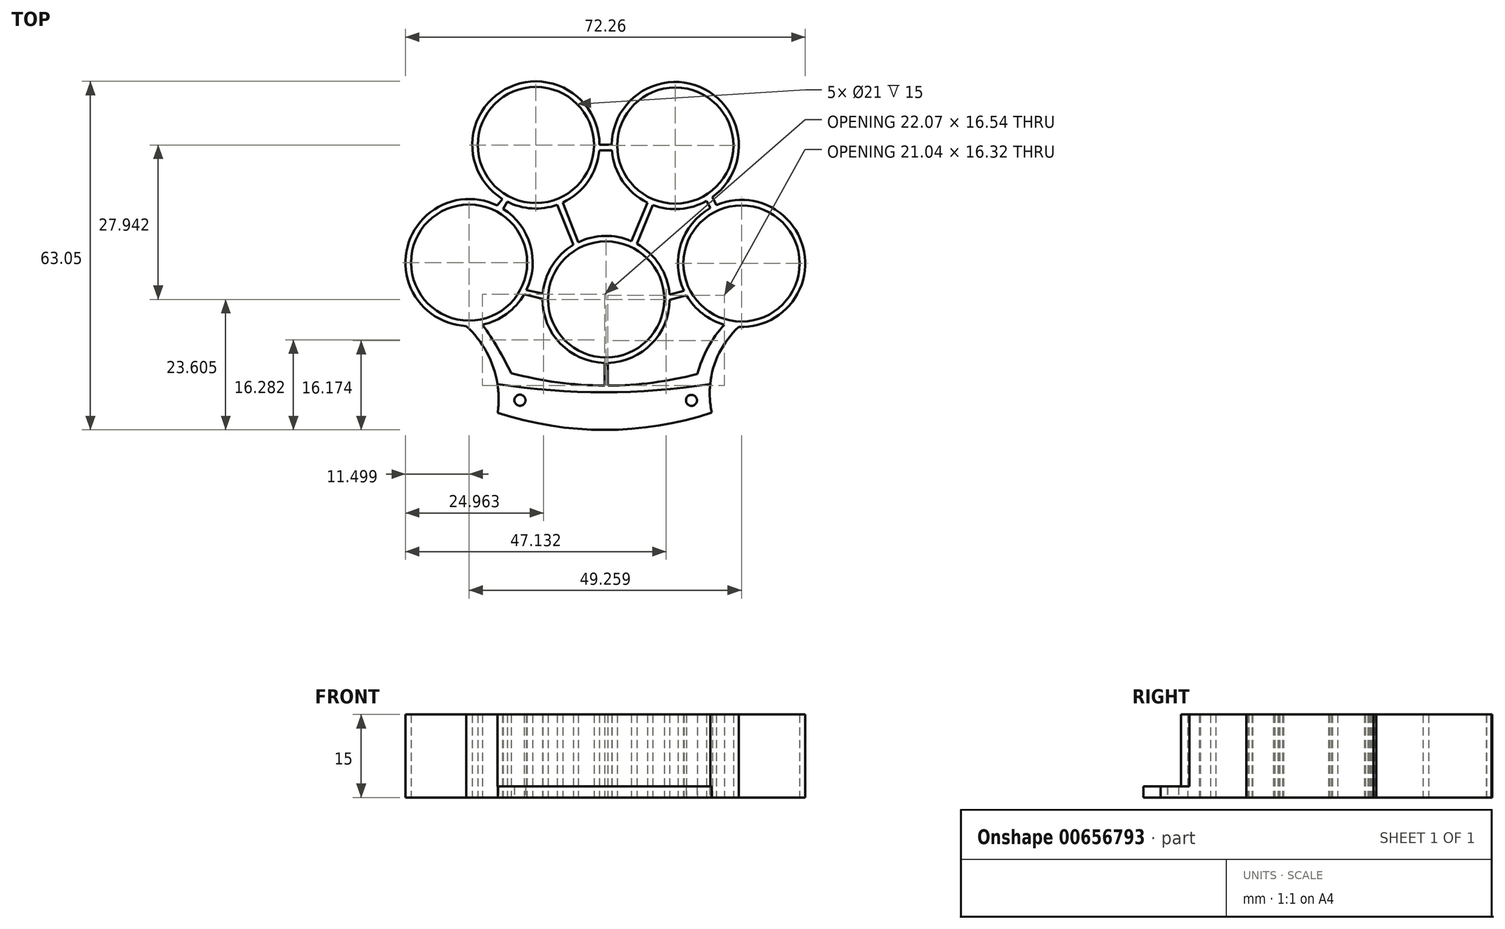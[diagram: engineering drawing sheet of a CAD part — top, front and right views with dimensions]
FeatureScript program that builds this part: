
annotation { "Feature Type Name" : "Feature", "Feature Type Description" : "" }
export const myFeature = defineFeature(function(context is Context, id is Id, definition is map)
    precondition{}
    {
        {
            var Q0;
            Q0=qCreatedBy(makeId("Top.planeOp"),FACE);
            var sketch = newSketch(context, id + "F0", { "sketchPlane" : qUnion([Q0])});
            skCircle(sketch, "E0", {"center": v(0, 0) * mm, "radius": 65 * mm, "construction": true});
            skCircle(sketch, "E1", {"center": v(0, 0) * mm, "radius": 49.37 * mm, "construction": true});
            skCircle(sketch, "E2", {"center": v(-24.77, -42.7) * mm, "radius": 10.5 * mm});
            skCircle(sketch, "E3", {"center": v(0, -49.37) * mm, "radius": 10.5 * mm});
            skCircle(sketch, "E4", {"center": v(24.49, -42.86) * mm, "radius": 10.5 * mm});
            skCircle(sketch, "E5", {"center": v(0, 0) * mm, "radius": 24.9 * mm, "construction": true});
            skLineSegment(sketch, "E6", {"start": v(0, 0) * mm, "end": v(95.97, 0) * mm, "construction": true});
            skLineSegment(sketch, "E7", {"start": v(0, 0) * mm, "end": v(-94.56, 0) * mm, "construction": true});
            skCircle(sketch, "E8", {"center": v(12.52, -21.53) * mm, "radius": 11.5 * mm});
            skCircle(sketch, "E9", {"center": v(-12.7, -21.42) * mm, "radius": 11.5 * mm});
            skLineSegment(sketch, "E10", {"start": v(-89.55, 88.06) * mm, "end": v(89.42, 88.01) * mm, "construction": true});
            skCircle(sketch, "E11", {"center": v(-15.57, -67.61) * mm, "radius": 1 * mm});
            skCircle(sketch, "E12", {"center": v(15.44, -67.63) * mm, "radius": 1 * mm});
            skCircle(sketch, "E13", {"center": v(24.49, -42.86) * mm, "radius": 11.5 * mm});
            skCircle(sketch, "E14", {"center": v(0, -49.37) * mm, "radius": 11.5 * mm});
            skCircle(sketch, "E15", {"center": v(-24.77, -42.7) * mm, "radius": 11.5 * mm});
            skCircle(sketch, "E16", {"center": v(-12.7, -21.42) * mm, "radius": 10.5 * mm});
            skCircle(sketch, "E17", {"center": v(12.52, -21.53) * mm, "radius": 10.5 * mm});
            skArc(sketch, "E18", {"start": v(-19.58, -69.88) * mm, "mid": v(-0.23, -72.97) * mm, "end": v(19.12, -69.83) * mm});
            skArc(sketch, "E19", {"start": v(-19.58, -69.88) * mm, "mid": v(-20.5, -61.33) * mm, "end": v(-25.28, -54.19) * mm});
            skArc(sketch, "E20", {"start": v(23.98, -54.35) * mm, "mid": v(19.48, -61.44) * mm, "end": v(19.12, -69.83) * mm});
            skArc(sketch, "E21", {"start": v(-17.15, -62.7) * mm, "mid": v(-0.33, -64.96) * mm, "end": v(16.5, -62.87) * mm});
            skLineSegment(sketch, "E22", {"start": v(-0.27, -60.86) * mm, "end": v(-0.27, -64.96) * mm});
            skLineSegment(sketch, "E23", {"start": v(0.34, -60.86) * mm, "end": v(0.34, -64.96) * mm});
            skArc(sketch, "E24", {"start": v(21.38, -53.94) * mm, "mid": v(18.4, -58.1) * mm, "end": v(16.5, -62.87) * mm});
            skArc(sketch, "E25", {"start": v(-17.15, -62.7) * mm, "mid": v(-19.57, -58.21) * mm, "end": v(-22.34, -53.94) * mm});
            skLineSegment(sketch, "E26", {"start": v(11.47, -48.51) * mm, "end": v(14.1, -47.8) * mm});
            skLineSegment(sketch, "E27", {"start": v(14.54, -48.63) * mm, "end": v(11.5, -49.47) * mm});
            skLineSegment(sketch, "E28", {"start": v(-14.4, -47.66) * mm, "end": v(-11.45, -48.32) * mm});
            skLineSegment(sketch, "E29", {"start": v(-14.8, -48.42) * mm, "end": v(-11.5, -49.26) * mm});
            skLineSegment(sketch, "E30", {"start": v(-1.2, -21.38) * mm, "end": v(1.02, -21.38) * mm});
            skLineSegment(sketch, "E31", {"start": v(1.05, -22.4) * mm, "end": v(-1.23, -22.4) * mm});
            skLineSegment(sketch, "E32", {"start": v(-19.67, -32.4) * mm, "end": v(-18.75, -31.2) * mm});
            skLineSegment(sketch, "E33", {"start": v(-17.88, -31.69) * mm, "end": v(-18.63, -32.98) * mm});
            skLineSegment(sketch, "E34", {"start": v(18.16, -31.54) * mm, "end": v(18.88, -32.83) * mm});
            skLineSegment(sketch, "E35", {"start": v(19.23, -30.86) * mm, "end": v(19.92, -32.3) * mm});
            skLineSegment(sketch, "E36", {"start": v(4.6, -38.82) * mm, "end": v(7.46, -31.85) * mm});
            skLineSegment(sketch, "E37", {"start": v(8.46, -32.29) * mm, "end": v(5.6, -39.32) * mm});
            skLineSegment(sketch, "E38", {"start": v(-5.03, -39.03) * mm, "end": v(-7.85, -31.85) * mm});
            skLineSegment(sketch, "E39", {"start": v(-8.85, -32.26) * mm, "end": v(-5.91, -39.5) * mm});
            skLineSegment(sketch, "E40", {"start": v(0, 0) * mm, "end": v(12.48, -6.94) * mm});
            skLineSegment(sketch, "E41", {"start": v(12.48, -6.94) * mm, "end": v(21.83, -11.98) * mm});
            skLineSegment(sketch, "E42", {"start": v(21.83, -11.98) * mm, "end": v(35.02, -34.8) * mm});
            skLineSegment(sketch, "E43", {"start": v(35.02, -34.8) * mm, "end": v(46.04, -45.89) * mm});
            skLineSegment(sketch, "E44", {"start": v(0, 0) * mm, "end": v(-21.9, -11.84) * mm});
            skLineSegment(sketch, "E45", {"start": v(-21.9, -11.84) * mm, "end": v(-35.08, -34.73) * mm});
            skLineSegment(sketch, "E46", {"start": v(-35.08, -34.73) * mm, "end": v(-46.2, -45.72) * mm});
            skLineSegment(sketch, "E47", {"start": v(-46.2, -45.72) * mm, "end": v(-49.24, -48.95) * mm});
            skLineSegment(sketch, "E48", {"start": v(-49.24, -48.95) * mm, "end": v(-19.58, -69.88) * mm});
            skLineSegment(sketch, "E49", {"start": v(46.04, -45.89) * mm, "end": v(48.99, -48.77) * mm});
            skLineSegment(sketch, "E50", {"start": v(48.99, -48.77) * mm, "end": v(19.12, -69.83) * mm});
            skSolve(sketch);
        }
        {
            var Q0;
            {var subQ0=sQuery(id+"F0.wireOp",EDGE,"E36");Q0=makeQuery(id+"F0.imprint","IMPRINT",FACE,{"disambiguationData":[TD([[makeQuery(id+"F0.imprint","IMPRINT",EDGE,{"derivedFrom":subQ0}),-1.0]])]});}
            var Q1;
            Q1=makeQuery(id+"F0.imprint","IMPRINT",FACE,{"disambiguationData":[TD([[makeQuery(id+"F0.imprint","IMPRINT",EDGE,{"derivedFrom":sQuery(id+"F0.wireOp",EDGE,"E3")}),-1.0]])]});
            var Q2;
            {var subQ0=sQuery(id+"F0.wireOp",EDGE,"E38");Q2=makeQuery(id+"F0.imprint","IMPRINT",FACE,{"disambiguationData":[TD([[makeQuery(id+"F0.imprint","IMPRINT",EDGE,{"derivedFrom":subQ0}),1.0]])]});}
            var Q3;
            {var subQ0=sQuery(id+"F0.wireOp",EDGE,"E28");Q3=makeQuery(id+"F0.imprint","IMPRINT",FACE,{"disambiguationData":[TD([[makeQuery(id+"F0.imprint","IMPRINT",EDGE,{"derivedFrom":subQ0}),-1.0]])]});}
            var Q4;
            {var subQ0=sQuery(id+"F0.wireOp",EDGE,"E22");Q4=makeQuery(id+"F0.imprint","IMPRINT",FACE,{"disambiguationData":[TD([[makeQuery(id+"F0.imprint","IMPRINT",EDGE,{"derivedFrom":subQ0}),1.0]])]});}
            var Q5;
            {var subQ0=sQuery(id+"F0.wireOp",EDGE,"E26");Q5=makeQuery(id+"F0.imprint","IMPRINT",FACE,{"disambiguationData":[TD([[makeQuery(id+"F0.imprint","IMPRINT",EDGE,{"derivedFrom":subQ0}),-1.0]])]});}
            var Q6;
            Q6 = qSketchRegion(id + "F2", true);
            var Q7;
            Q7=makeQuery(id+"F0.imprint","IMPRINT",FACE,{"disambiguationData":[TD([[makeQuery(id+"F0.imprint","IMPRINT",EDGE,{"derivedFrom":sQuery(id+"F0.wireOp",EDGE,"E2")}),-1.0]])]});
            var Q8;
            Q8=makeQuery(id+"F0.imprint","IMPRINT",FACE,{"disambiguationData":[TD([[makeQuery(id+"F0.imprint","IMPRINT",EDGE,{"derivedFrom":sQuery(id+"F0.wireOp",EDGE,"E11")}),-1.0]])]});
            var Q9;
            Q9=makeQuery(id+"F0.imprint","IMPRINT",FACE,{"disambiguationData":[TD([[makeQuery(id+"F0.imprint","IMPRINT",EDGE,{"derivedFrom":sQuery(id+"F0.wireOp",EDGE,"E16")}),-1.0]])]});
            var Q10;
            {var subQ0=sQuery(id+"F0.wireOp",EDGE,"E32");Q10=makeQuery(id+"F0.imprint","IMPRINT",FACE,{"disambiguationData":[TD([[makeQuery(id+"F0.imprint","IMPRINT",EDGE,{"derivedFrom":subQ0}),-1.0]])]});}
            var Q11;
            {var subQ0=sQuery(id+"F0.wireOp",EDGE,"E30");Q11=makeQuery(id+"F0.imprint","IMPRINT",FACE,{"disambiguationData":[TD([[makeQuery(id+"F0.imprint","IMPRINT",EDGE,{"derivedFrom":subQ0}),-1.0]])]});}
            var Q12;
            Q12=makeQuery(id+"F0.imprint","IMPRINT",FACE,{"disambiguationData":[TD([[makeQuery(id+"F0.imprint","IMPRINT",EDGE,{"derivedFrom":sQuery(id+"F0.wireOp",EDGE,"E17")}),-1.0]])]});
            var Q13;
            {var subQ0=sQuery(id+"F0.wireOp",EDGE,"E34");Q13=makeQuery(id+"F0.imprint","IMPRINT",FACE,{"disambiguationData":[TD([[makeQuery(id+"F0.imprint","IMPRINT",EDGE,{"derivedFrom":subQ0}),1.0]])]});}
            var Q14;
            Q14=makeQuery(id+"F0.imprint","IMPRINT",FACE,{"disambiguationData":[TD([[makeQuery(id+"F0.imprint","IMPRINT",EDGE,{"derivedFrom":sQuery(id+"F0.wireOp",EDGE,"E4")}),-1.0]])]});
            extrude(context, id + "F1", {"entities" : qUnion([Q0, Q1, Q2, Q3, Q4, Q5, Q6, Q7, Q8, Q9, Q10, Q11, Q12, Q13, Q14]), "depth" : 15 * mm, "offsetDistance" : 25 * mm});
        }
        {
            var Q0;
            Q0=makeQuery(id+"F1.opExtrude","CAP_FACE",FACE,{"disambiguationData":[OSD([sQuery(id+"F0.wireOp",EDGE,"E2"),sQuery(id+"F0.wireOp",EDGE,"E3"),sQuery(id+"F0.wireOp",EDGE,"E4"),sQuery(id+"F0.wireOp",EDGE,"E8"),sQuery(id+"F0.wireOp",EDGE,"E9"),sQuery(id+"F0.wireOp",EDGE,"E11"),sQuery(id+"F0.wireOp",EDGE,"E12"),sQuery(id+"F0.wireOp",EDGE,"E13"),sQuery(id+"F0.wireOp",EDGE,"E14"),sQuery(id+"F0.wireOp",EDGE,"E15"),sQuery(id+"F0.wireOp",EDGE,"E16"),sQuery(id+"F0.wireOp",EDGE,"E17"),sQuery(id+"F0.wireOp",EDGE,"E18"),sQuery(id+"F0.wireOp",EDGE,"E19"),sQuery(id+"F0.wireOp",EDGE,"E20"),sQuery(id+"F0.wireOp",EDGE,"E21"),sQuery(id+"F0.wireOp",EDGE,"E22"),sQuery(id+"F0.wireOp",EDGE,"E23"),sQuery(id+"F0.wireOp",EDGE,"E24"),sQuery(id+"F0.wireOp",EDGE,"E25"),sQuery(id+"F0.wireOp",EDGE,"E26"),sQuery(id+"F0.wireOp",EDGE,"E27"),sQuery(id+"F0.wireOp",EDGE,"E28"),sQuery(id+"F0.wireOp",EDGE,"E29"),sQuery(id+"F0.wireOp",EDGE,"E30"),sQuery(id+"F0.wireOp",EDGE,"E31"),sQuery(id+"F0.wireOp",EDGE,"E32"),sQuery(id+"F0.wireOp",EDGE,"E33"),sQuery(id+"F0.wireOp",EDGE,"E34"),sQuery(id+"F0.wireOp",EDGE,"E35"),sQuery(id+"F0.wireOp",EDGE,"E36"),sQuery(id+"F0.wireOp",EDGE,"E37"),sQuery(id+"F0.wireOp",EDGE,"E38"),sQuery(id+"F0.wireOp",EDGE,"E39")])],"isStart":false});
            var sketch = newSketch(context, id + "F2", { "sketchPlane" : qUnion([Q0])});
            skArc(sketch, "E51", {"start": v(-25.47, -67.6) * mm, "mid": v(-0.24, -73.33) * mm, "end": v(24.99, -67.55) * mm});
            skLineSegment(sketch, "E52", {"start": v(-25.47, -67.6) * mm, "end": v(-25.47, -63.6) * mm});
            skLineSegment(sketch, "E53", {"start": v(24.99, -67.55) * mm, "end": v(24.99, -63.55) * mm});
            skArc(sketch, "E54", {"start": v(-25.47, -63.6) * mm, "mid": v(-0.24, -66.16) * mm, "end": v(24.99, -63.55) * mm});
            skSolve(sketch);
        }
        {
            var Q0;
            Q0 = qSketchRegion(id + "F2", true);
            extrude(context, id + "F3", {"entities" : qUnion([Q0]), "operationType" : NewBodyOperationType.REMOVE, "oppositeDirection" : true, "depth" : 13 * mm, "offsetDistance" : 25 * mm});
        }
    });
